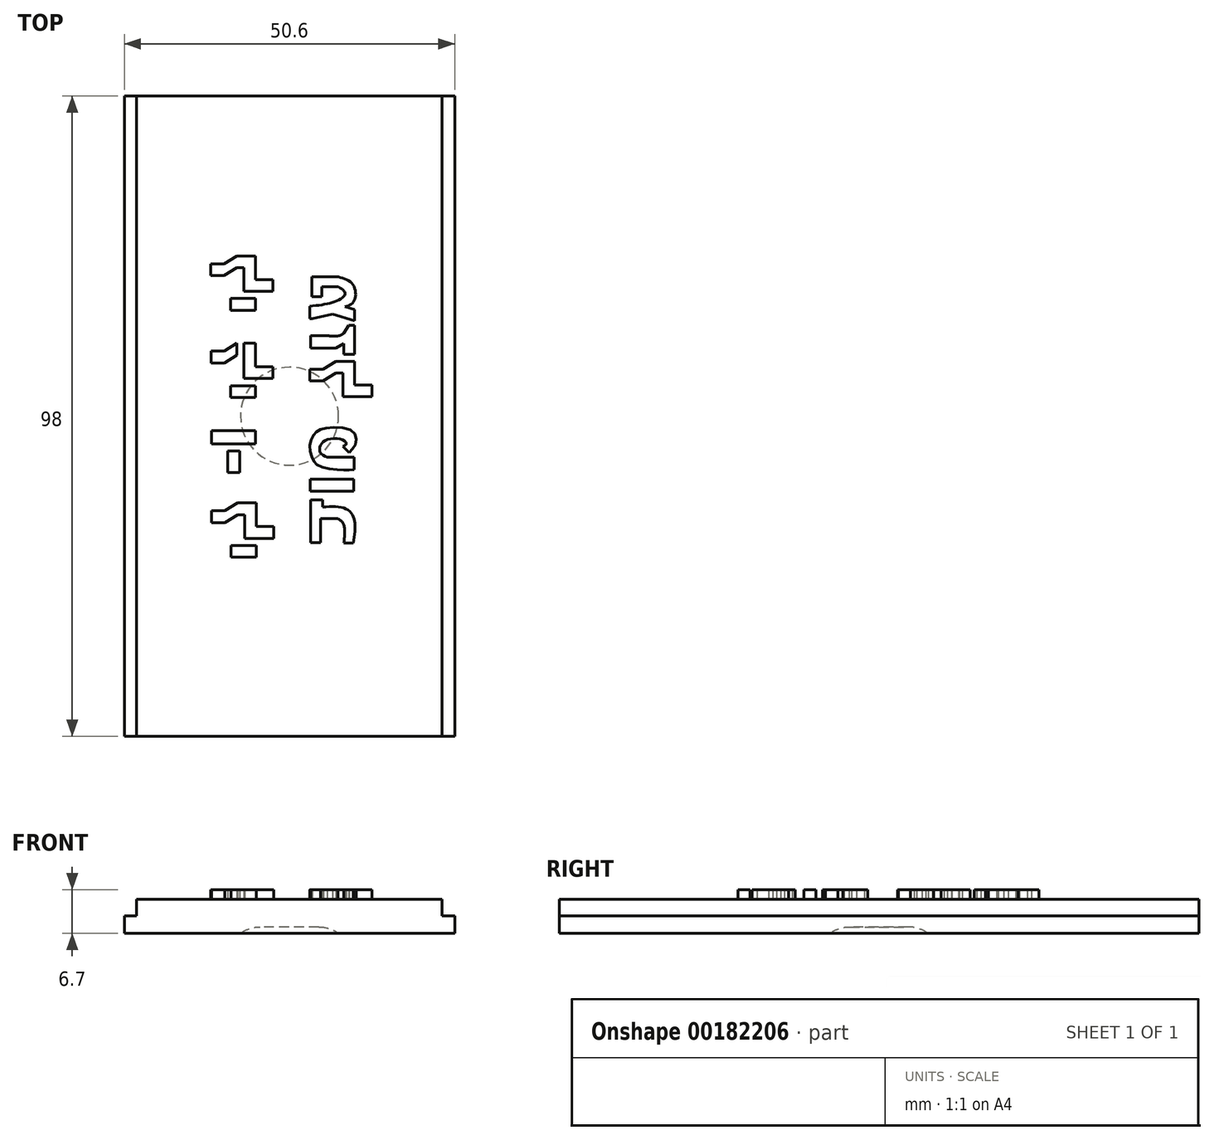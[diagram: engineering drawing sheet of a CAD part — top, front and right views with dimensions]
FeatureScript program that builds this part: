
annotation { "Feature Type Name" : "Feature", "Feature Type Description" : "" }
export const myFeature = defineFeature(function(context is Context, id is Id, definition is map)
    precondition{}
    {
        {
            var Q0;
            Q0=qCreatedBy(makeId("Front.planeOp"),FACE);
            var sketch = newSketch(context, id + "F0", { "sketchPlane" : qUnion([Q0])});
            skLineSegment(sketch, "E0.bottom", {"start": v(25.3, 1.35) * mm, "end": v(-25.3, 1.35) * mm});
            skLineSegment(sketch, "E0.top", {"start": v(25.3, -1.35) * mm, "end": v(-25.3, -1.35) * mm});
            skLineSegment(sketch, "E0.left", {"start": v(25.3, 1.35) * mm, "end": v(25.3, -1.35) * mm});
            skLineSegment(sketch, "E0.right", {"start": v(-25.3, 1.35) * mm, "end": v(-25.3, -1.35) * mm});
            skPoint(sketch, "E0.middle", {"position": v(0, 0) * mm});
            skLineSegment(sketch, "E1", {"start": v(-25.3, 1.35) * mm, "end": v(-23.45, 1.35) * mm});
            skLineSegment(sketch, "E2", {"start": v(25.3, 1.35) * mm, "end": v(23.35, 1.35) * mm});
            skLineSegment(sketch, "E3", {"start": v(-23.45, 1.35) * mm, "end": v(-23.45, 3.85) * mm});
            skLineSegment(sketch, "E4", {"start": v(-23.45, 3.85) * mm, "end": v(23.35, 3.85) * mm});
            skLineSegment(sketch, "E5", {"start": v(23.35, 3.85) * mm, "end": v(23.35, 1.35) * mm});
            skSolve(sketch);
        }
        {
            var Q0;
            Q0=makeQuery(id+"F0.imprint","IMPRINT",FACE,{"disambiguationData":[TD([[makeQuery(id+"F0.imprint","IMPRINT",EDGE,{"derivedFrom":sQuery(id+"F0.wireOp",EDGE,"E0.bottom")}),1.0]])]});
            var Q1;
            Q1=makeQuery(id+"F0.imprint","IMPRINT",FACE,{"disambiguationData":[TD([[makeQuery(id+"F0.imprint","IMPRINT",EDGE,{"derivedFrom":sQuery(id+"F0.wireOp",EDGE,"E0.bottom")}),-1.0]])]});
            extrude(context, id + "F1", {"entities" : qUnion([Q0, Q1]), "endBound" : BoundingType.SYMMETRIC, "depth" : 98 * mm});
        }
        {
            var Q0;
            Q0=qCreatedBy(makeId("Front.planeOp"),FACE);
            var sketch = newSketch(context, id + "F2", { "sketchPlane" : qUnion([Q0])});
            skLineSegment(sketch, "E6.bottom", {"start": v(0, -0.35) * mm, "end": v(7.5, -0.35) * mm});
            skLineSegment(sketch, "E6.top", {"start": v(0, -1.35) * mm, "end": v(7.5, -1.35) * mm});
            skLineSegment(sketch, "E6.left", {"start": v(0, -0.35) * mm, "end": v(0, -1.35) * mm});
            skLineSegment(sketch, "E6.right", {"start": v(7.5, -0.35) * mm, "end": v(7.5, -1.35) * mm});
            skSolve(sketch);
        }
        {
            var Q0;
            Q0=qSketchRegion(id+"F2",true);
            var Q1;
            Q1=sQuery(id+"F2.wireOp",EDGE,"E6.left");
            revolve(context, id + "F3", {"operationType" : NewBodyOperationType.REMOVE, "entities" : qUnion([Q0]), "axis" : qUnion([Q1]), "revolveType" : RevolveType.FULL});
        }
        {
            var Q0;
            Q0=makeQuery(id+"F3.boolean.opBoolean","COPY",EDGE,{"derivedFrom":makeQuery(id+"F3.opRevolve","SWEPT_EDGE",EDGE,{"disambiguationData":[OSD([sQuery(id+"F2.wireOp",EDGE,"E6.bottom"),sQuery(id+"F2.wireOp",EDGE,"E6.right")])]})});
            fillet(context, id + "F4", {"entities" : qUnion([Q0]), "radius" : 5 * mm, "tangentPropagation" : true, "allowEdgeOverflow" : false});
        }
        {
            var Q0;
            Q0=makeQuery(id+"F1.opExtrude","SWEPT_FACE",FACE,{"disambiguationData":[OSD([sQuery(id+"F0.wireOp",EDGE,"E4")])]});
            var sketch = newSketch(context, id + "F5", { "sketchPlane" : qUnion([Q0])});
            skLineSegment(sketch, "E7.MirrorCS", {"start": v(-5.1, -21.59) * mm, "end": v(-8.93, -21.59) * mm});
            skLineSegment(sketch, "E8.MirrorCS", {"start": v(-5.1, -21.59) * mm, "end": v(-5.1, -19.78) * mm});
            skLineSegment(sketch, "E9.MirrorCS", {"start": v(-5.1, -19.78) * mm, "end": v(-8.93, -19.78) * mm});
            skLineSegment(sketch, "E10.MirrorCS", {"start": v(-8.93, -21.59) * mm, "end": v(-8.93, -19.78) * mm});
            skLineSegment(sketch, "E11.MirrorCS", {"start": v(-2.43, -18.7) * mm, "end": v(-6.89, -18.7) * mm});
            skLineSegment(sketch, "E12.MirrorCS", {"start": v(-2.43, -18.7) * mm, "end": v(-2.43, -16.9) * mm});
            skLineSegment(sketch, "E13.MirrorCS", {"start": v(-2.43, -16.9) * mm, "end": v(-6.89, -16.9) * mm});
            skLineSegment(sketch, "E14.MirrorCS", {"start": v(-6.89, -18.7) * mm, "end": v(-6.89, -16.9) * mm});
            skLineSegment(sketch, "E15.MirrorCS", {"start": v(-6.89, -16.9) * mm, "end": v(-6.89, -13.28) * mm});
            skLineSegment(sketch, "E16.MirrorCS", {"start": v(-5.1, -16.9) * mm, "end": v(-5.1, -13.28) * mm});
            skLineSegment(sketch, "E17.MirrorCS", {"start": v(-6.89, -13.28) * mm, "end": v(-5.1, -13.28) * mm});
            skLineSegment(sketch, "E18.MirrorCS", {"start": v(-6.89, -15.09) * mm, "end": v(-7.97, -15.09) * mm});
            skLineSegment(sketch, "E19.MirrorCS", {"start": v(-6.89, -13.28) * mm, "end": v(-7.97, -13.28) * mm});
            skLineSegment(sketch, "E20.MirrorCS", {"start": v(-9.9, -16.29) * mm, "end": v(-7.97, -15.09) * mm});
            skLineSegment(sketch, "E21.MirrorCS", {"start": v(-7.97, -13.28) * mm, "end": v(-9.9, -14.48) * mm});
            skLineSegment(sketch, "E22.MirrorCS", {"start": v(-11.94, -16.29) * mm, "end": v(-11.94, -14.48) * mm});
            skLineSegment(sketch, "E23.MirrorCS", {"start": v(-9.9, -16.29) * mm, "end": v(-11.94, -16.29) * mm});
            skLineSegment(sketch, "E24.MirrorCS", {"start": v(-9.9, -14.48) * mm, "end": v(-11.94, -14.48) * mm});
            skLineSegment(sketch, "E25.MirrorCS", {"start": v(-5.19, -2.22) * mm, "end": v(-11.97, -2.22) * mm});
            skLineSegment(sketch, "E26.MirrorCS", {"start": v(-5.19, -4.22) * mm, "end": v(-11.97, -4.22) * mm});
            skLineSegment(sketch, "E27.MirrorCS", {"start": v(-11.97, -4.22) * mm, "end": v(-11.97, -2.22) * mm});
            skLineSegment(sketch, "E28.MirrorCS", {"start": v(-5.19, -4.22) * mm, "end": v(-5.19, -2.22) * mm});
            skLineSegment(sketch, "E29.MirrorCS", {"start": v(-7.64, -8.65) * mm, "end": v(-9.48, -8.65) * mm});
            skLineSegment(sketch, "E30.MirrorCS", {"start": v(-7.64, -8.65) * mm, "end": v(-7.64, -5.33) * mm});
            skLineSegment(sketch, "E31.MirrorCS", {"start": v(-9.48, -8.65) * mm, "end": v(-9.48, -5.33) * mm});
            skLineSegment(sketch, "E32.MirrorCS", {"start": v(-7.64, -5.33) * mm, "end": v(-9.48, -5.33) * mm});
            skLineSegment(sketch, "E33.MirrorCS", {"start": v(-5.19, 2.87) * mm, "end": v(-9.02, 2.87) * mm});
            skLineSegment(sketch, "E34.MirrorCS", {"start": v(-5.19, 2.87) * mm, "end": v(-5.19, 4.67) * mm});
            skLineSegment(sketch, "E35.MirrorCS", {"start": v(-9.02, 2.87) * mm, "end": v(-9.02, 4.67) * mm});
            skLineSegment(sketch, "E36.MirrorCS", {"start": v(-5.19, 4.67) * mm, "end": v(-9.02, 4.67) * mm});
            skLineSegment(sketch, "E37.MirrorCS", {"start": v(-2.52, 5.76) * mm, "end": v(-6.98, 5.76) * mm});
            skLineSegment(sketch, "E38.MirrorCS", {"start": v(-2.52, 5.76) * mm, "end": v(-2.52, 7.56) * mm});
            skLineSegment(sketch, "E39.MirrorCS", {"start": v(-6.98, 5.76) * mm, "end": v(-6.98, 7.56) * mm});
            skLineSegment(sketch, "E40.MirrorCS", {"start": v(-5.19, 7.56) * mm, "end": v(-5.19, 11.17) * mm});
            skLineSegment(sketch, "E41.MirrorCS", {"start": v(-6.98, 7.56) * mm, "end": v(-6.98, 11.17) * mm});
            skLineSegment(sketch, "E42.MirrorCS", {"start": v(-6.98, 7.56) * mm, "end": v(-5.19, 7.56) * mm});
            skLineSegment(sketch, "E43.MirrorCS", {"start": v(-2.52, 7.56) * mm, "end": v(-6.98, 7.56) * mm});
            skLineSegment(sketch, "E44.MirrorCS", {"start": v(-6.98, 11.17) * mm, "end": v(-6.98, 9.37) * mm});
            skLineSegment(sketch, "E45.MirrorCS", {"start": v(-8.06, 11.17) * mm, "end": v(-8.06, 9.37) * mm});
            skLineSegment(sketch, "E46.MirrorCS", {"start": v(-6.98, 11.17) * mm, "end": v(-8.06, 11.17) * mm});
            skLineSegment(sketch, "E47.MirrorCS", {"start": v(-6.98, 9.37) * mm, "end": v(-8.06, 9.37) * mm});
            skLineSegment(sketch, "E48.MirrorCS", {"start": v(-8.06, 11.17) * mm, "end": v(-9.99, 9.97) * mm});
            skLineSegment(sketch, "E49.MirrorCS", {"start": v(-9.99, 8.16) * mm, "end": v(-8.06, 9.37) * mm});
            skLineSegment(sketch, "E50.MirrorCS", {"start": v(-9.99, 8.16) * mm, "end": v(-12.03, 8.16) * mm});
            skLineSegment(sketch, "E51.MirrorCS", {"start": v(-9.99, 9.97) * mm, "end": v(-12.03, 9.97) * mm});
            skLineSegment(sketch, "E52.MirrorCS", {"start": v(-12.03, 8.16) * mm, "end": v(-12.03, 9.97) * mm});
            skLineSegment(sketch, "E53.MirrorCS", {"start": v(-6.98, 11.17) * mm, "end": v(-5.19, 11.17) * mm});
            skLineSegment(sketch, "E54.MirrorCS", {"start": v(-2.55, 19.11) * mm, "end": v(-2.55, 20.92) * mm});
            skLineSegment(sketch, "E55.MirrorCS", {"start": v(-2.55, 19.11) * mm, "end": v(-7, 19.11) * mm});
            skLineSegment(sketch, "E56.MirrorCS", {"start": v(-2.55, 20.92) * mm, "end": v(-7, 20.92) * mm});
            skLineSegment(sketch, "E57.MirrorCS", {"start": v(-5.22, 20.92) * mm, "end": v(-5.22, 24.53) * mm});
            skLineSegment(sketch, "E58.MirrorCS", {"start": v(-7, 24.53) * mm, "end": v(-5.22, 24.53) * mm});
            skLineSegment(sketch, "E59.MirrorCS", {"start": v(-7, 20.92) * mm, "end": v(-7, 24.53) * mm});
            skLineSegment(sketch, "E60.MirrorCS", {"start": v(-7, 19.11) * mm, "end": v(-7, 20.92) * mm});
            skLineSegment(sketch, "E61.MirrorCS", {"start": v(-7, 22.72) * mm, "end": v(-8.09, 22.72) * mm});
            skLineSegment(sketch, "E62.MirrorCS", {"start": v(-7, 24.53) * mm, "end": v(-8.09, 24.53) * mm});
            skLineSegment(sketch, "E63.MirrorCS", {"start": v(-8.09, 24.53) * mm, "end": v(-10.02, 23.33) * mm});
            skLineSegment(sketch, "E64.MirrorCS", {"start": v(-10.02, 21.52) * mm, "end": v(-8.09, 22.72) * mm});
            skLineSegment(sketch, "E65.MirrorCS", {"start": v(-10.02, 21.52) * mm, "end": v(-12.06, 21.52) * mm});
            skLineSegment(sketch, "E66.MirrorCS", {"start": v(-10.02, 23.33) * mm, "end": v(-12.06, 23.33) * mm});
            skLineSegment(sketch, "E67.MirrorCS", {"start": v(-12.06, 21.52) * mm, "end": v(-12.06, 23.33) * mm});
            skLineSegment(sketch, "E68.MirrorCS", {"start": v(-5.22, 18.03) * mm, "end": v(-9.05, 18.03) * mm});
            skLineSegment(sketch, "E69.MirrorCS", {"start": v(-9.05, 16.22) * mm, "end": v(-9.05, 18.03) * mm});
            skLineSegment(sketch, "E70.MirrorCS", {"start": v(-5.22, 16.22) * mm, "end": v(-9.05, 16.22) * mm});
            skLineSegment(sketch, "E71.MirrorCS", {"start": v(-5.22, 16.22) * mm, "end": v(-5.22, 18.03) * mm});
            skFitSpline(sketch, "E72.MirrorCS", {"points": [v(7.5, 19.8) * mm, v(8.5, 18.86) * mm, v(7.5, 17.76) * mm, v(3.11, 16.82) * mm], "startDerivative": vector(5.52, -3.39) * mm, "endDerivative": vector(-10.58, -1.26) * mm});
            skLineSegment(sketch, "E73.MirrorCS", {"start": v(4.92, 19.8) * mm, "end": v(7.5, 19.8) * mm});
            skLineSegment(sketch, "E74.MirrorCS", {"start": v(4.92, 18.27) * mm, "end": v(4.92, 19.8) * mm});
            skLineSegment(sketch, "E75.MirrorCS", {"start": v(3.4, 18.27) * mm, "end": v(4.92, 18.27) * mm});
            skLineSegment(sketch, "E76.MirrorCS", {"start": v(3.4, 21.33) * mm, "end": v(3.4, 18.27) * mm});
            skLineSegment(sketch, "E77.MirrorCS", {"start": v(7.5, 21.33) * mm, "end": v(3.4, 21.33) * mm});
            skFitSpline(sketch, "E78.MirrorCS", {"points": [v(8.53, 16.75) * mm, v(9.86, 17.59) * mm, v(9.78, 20.06) * mm, v(7.5, 21.33) * mm], "startDerivative": vector(5.55, 1.8) * mm, "endDerivative": vector(-7.52, 2.27) * mm});
            skLineSegment(sketch, "E79.MirrorCS", {"start": v(9.96, 14.6) * mm, "end": v(9.96, 16.3) * mm});
            skLineSegment(sketch, "E80.MirrorCS", {"start": v(9.96, 16.3) * mm, "end": v(8.53, 16.75) * mm});
            skLineSegment(sketch, "E81.MirrorCS", {"start": v(6.62, 15.63) * mm, "end": v(9.96, 14.6) * mm});
            skFitSpline(sketch, "E82.MirrorCS", {"points": [v(3.48, 14.95) * mm, v(6.62, 15.63) * mm], "startDerivative": vector(3.15, 0.68) * mm, "endDerivative": vector(3.15, 0.68) * mm});
            skLineSegment(sketch, "E83.MirrorCS", {"start": v(3.11, 16.82) * mm, "end": v(3.11, 14.95) * mm});
            skLineSegment(sketch, "E84.MirrorCS", {"start": v(3.48, 14.95) * mm, "end": v(3.11, 14.95) * mm});
            skFitSpline(sketch, "E85.MirrorCS", {"points": [v(3.48, 14.95) * mm, v(6.62, 15.63) * mm], "startDerivative": vector(3.15, 0.68) * mm, "endDerivative": vector(3.15, 0.68) * mm});
            skLineSegment(sketch, "E86.MirrorCS", {"start": v(3.22, 12.3) * mm, "end": v(5.18, 12.3) * mm});
            skFitSpline(sketch, "E87.MirrorCS", {"points": [v(5.18, 12.3) * mm, v(5.95, 12.3) * mm, v(7.5, 12.3) * mm, v(8.33, 12.73) * mm], "startDerivative": vector(2.37, 0.09) * mm, "endDerivative": vector(2.29, 1.69) * mm});
            skFitSpline(sketch, "E88.MirrorCS", {"points": [v(8.33, 12.73) * mm, v(9.06, 13.93) * mm], "startDerivative": vector(0.73, 1.2) * mm, "endDerivative": vector(0.73, 1.2) * mm});
            skLineSegment(sketch, "E89.MirrorCS", {"start": v(9.96, 13.93) * mm, "end": v(9.06, 13.93) * mm});
            skLineSegment(sketch, "E90.MirrorCS", {"start": v(9.96, 13.93) * mm, "end": v(9.96, 9.5) * mm});
            skLineSegment(sketch, "E91.MirrorCS", {"start": v(9.96, 9.5) * mm, "end": v(9.06, 9.5) * mm});
            skLineSegment(sketch, "E92.MirrorCS", {"start": v(9.06, 9.5) * mm, "end": v(8.33, 9.5) * mm});
            skLineSegment(sketch, "E93.MirrorCS", {"start": v(8.33, 9.5) * mm, "end": v(8.33, 12.73) * mm});
            skFitSpline(sketch, "E94.MirrorCS", {"points": [v(7.09, 10.43) * mm, v(5.67, 10.43) * mm, v(3.99, 10.43) * mm], "startDerivative": vector(-2.9, 0) * mm, "endDerivative": vector(-3.29, 0) * mm});
            skLineSegment(sketch, "E95.MirrorCS", {"start": v(3.99, 10.43) * mm, "end": v(3.22, 10.43) * mm});
            skLineSegment(sketch, "E96.MirrorCS", {"start": v(3.22, 10.43) * mm, "end": v(3.22, 12.3) * mm});
            skFitSpline(sketch, "E97.MirrorCS", {"points": [v(7.09, 10.43) * mm, v(8.33, 11.12) * mm], "startDerivative": vector(1.24, 0.68) * mm, "endDerivative": vector(1.24, 0.68) * mm});
            skLineSegment(sketch, "E98.MirrorCS", {"start": v(7.09, 8.4) * mm, "end": v(5.16, 7.2) * mm});
            skLineSegment(sketch, "E99.MirrorCS", {"start": v(5.16, 5.39) * mm, "end": v(7.09, 6.59) * mm});
            skLineSegment(sketch, "E100.MirrorCS", {"start": v(5.16, 5.39) * mm, "end": v(3.11, 5.39) * mm});
            skLineSegment(sketch, "E101.MirrorCS", {"start": v(5.16, 7.2) * mm, "end": v(3.11, 7.2) * mm});
            skLineSegment(sketch, "E102.MirrorCS", {"start": v(3.11, 5.39) * mm, "end": v(3.11, 7.2) * mm});
            skLineSegment(sketch, "E103.MirrorCS", {"start": v(5.16, 5.39) * mm, "end": v(5.16, 7.2) * mm});
            skLineSegment(sketch, "E104.MirrorCS", {"start": v(8.17, 6.59) * mm, "end": v(7.09, 6.59) * mm});
            skLineSegment(sketch, "E105.MirrorCS", {"start": v(8.17, 8.4) * mm, "end": v(7.09, 8.4) * mm});
            skLineSegment(sketch, "E106.MirrorCS", {"start": v(8.17, 8.4) * mm, "end": v(9.96, 8.4) * mm});
            skLineSegment(sketch, "E107.MirrorCS", {"start": v(9.96, 4.78) * mm, "end": v(9.96, 8.4) * mm});
            skLineSegment(sketch, "E108.MirrorCS", {"start": v(12.63, 4.78) * mm, "end": v(8.17, 4.78) * mm});
            skLineSegment(sketch, "E109.MirrorCS", {"start": v(8.17, 4.78) * mm, "end": v(8.17, 8.4) * mm});
            skLineSegment(sketch, "E110.MirrorCS", {"start": v(8.17, 2.98) * mm, "end": v(8.17, 4.78) * mm});
            skLineSegment(sketch, "E111.MirrorCS", {"start": v(12.63, 2.98) * mm, "end": v(8.17, 2.98) * mm});
            skLineSegment(sketch, "E112.MirrorCS", {"start": v(12.63, 2.98) * mm, "end": v(12.63, 4.78) * mm});
            skFitSpline(sketch, "E113.MirrorCS", {"points": [v(9.16, -5.56) * mm, v(10.12, -4.24) * mm, v(9.64, -2.31) * mm, v(5.42, -1.83) * mm, v(3.98, -2.55) * mm, v(3.14, -4.24) * mm, v(3.5, -6.4) * mm, v(4.46, -7.6) * mm, v(7.95, -8.21) * mm, v(9.88, -8.21) * mm], "startDerivative": vector(12.28, 12.03) * mm, "endDerivative": vector(16.13, 0.48) * mm});
            skLineSegment(sketch, "E114.MirrorCS", {"start": v(9.88, -8.21) * mm, "end": v(9.88, -6.28) * mm});
            skLineSegment(sketch, "E115.MirrorCS", {"start": v(5.79, -6.28) * mm, "end": v(9.64, -6.28) * mm});
            skLineSegment(sketch, "E116.MirrorCS", {"start": v(9.88, -6.28) * mm, "end": v(9.64, -6.28) * mm});
            skFitSpline(sketch, "E117.MirrorCS", {"points": [v(5.79, -6.28) * mm, v(4.7, -5.56) * mm, v(4.7, -4.6) * mm, v(5.67, -3.64) * mm, v(8.2, -3.64) * mm, v(8.68, -4.24) * mm, v(8.2, -4.6) * mm], "startDerivative": vector(-7.7, 3.48) * mm, "endDerivative": vector(-5.56, -2.54) * mm});
            skLineSegment(sketch, "E118.MirrorCS", {"start": v(9.16, -5.56) * mm, "end": v(8.2, -4.6) * mm});
            skLineSegment(sketch, "E119.MirrorCS", {"start": v(9.82, -9.66) * mm, "end": v(3.18, -9.66) * mm});
            skLineSegment(sketch, "E120.MirrorCS", {"start": v(3.18, -11.5) * mm, "end": v(3.18, -9.66) * mm});
            skLineSegment(sketch, "E121.MirrorCS", {"start": v(9.82, -11.5) * mm, "end": v(3.18, -11.5) * mm});
            skLineSegment(sketch, "E122.MirrorCS", {"start": v(9.82, -11.5) * mm, "end": v(9.82, -9.66) * mm});
            skLineSegment(sketch, "E123.MirrorCS", {"start": v(3.22, -12.8) * mm, "end": v(3.22, -19.37) * mm});
            skLineSegment(sketch, "E124.MirrorCS", {"start": v(4.75, -15.7) * mm, "end": v(7.4, -15.7) * mm});
            skLineSegment(sketch, "E125.MirrorCS", {"start": v(4.75, -19.37) * mm, "end": v(4.75, -15.7) * mm});
            skLineSegment(sketch, "E126.MirrorCS", {"start": v(3.22, -19.37) * mm, "end": v(4.75, -19.37) * mm});
            skFitSpline(sketch, "E127.MirrorCS", {"points": [v(7.4, -15.7) * mm, v(8.24, -16.47) * mm, v(8.33, -19.45) * mm], "startDerivative": vector(2.62, -1.46) * mm, "endDerivative": vector(-0.5, -5.7) * mm});
            skLineSegment(sketch, "E128.MirrorCS", {"start": v(9.78, -19.45) * mm, "end": v(8.33, -19.45) * mm});
            skFitSpline(sketch, "E129.MirrorCS", {"points": [v(9.78, -19.45) * mm, v(10.03, -16.64) * mm, v(9.6, -15.02) * mm, v(8.16, -14) * mm, v(5.1, -13.92) * mm], "startDerivative": vector(1.5, 10.74) * mm, "endDerivative": vector(-11.49, -0.83) * mm});
            skLineSegment(sketch, "E130.MirrorCS", {"start": v(5.1, -13.92) * mm, "end": v(5.1, -12.8) * mm});
            skLineSegment(sketch, "E131.MirrorCS", {"start": v(5.1, -12.8) * mm, "end": v(3.22, -12.8) * mm});
            skSolve(sketch);
        }
        {
            var Q0;
            Q0=makeQuery(id+"F5.imprint","IMPRINT",FACE,{"disambiguationData":[TD([[makeQuery(id+"F5.imprint","IMPRINT",EDGE,{"derivedFrom":sQuery(id+"F5.wireOp",EDGE,"E72.MirrorCS")}),1.0]])]});
            var Q1;
            Q1=makeQuery(id+"F5.imprint","IMPRINT",FACE,{"disambiguationData":[TD([[makeQuery(id+"F5.imprint","IMPRINT",EDGE,{"derivedFrom":sQuery(id+"F5.wireOp",EDGE,"E86.MirrorCS")}),-1.0]])]});
            var Q2;
            {var subQ0=sQuery(id+"F5.wireOp",EDGE,"E88.MirrorCS");Q2=makeQuery(id+"F5.imprint","IMPRINT",FACE,{"disambiguationData":[TD([[makeQuery(id+"F5.imprint","IMPRINT",EDGE,{"derivedFrom":subQ0}),-1.0]])]});}
            var Q3;
            Q3=makeQuery(id+"F5.imprint","IMPRINT",FACE,{"disambiguationData":[TD([[makeQuery(id+"F5.imprint","IMPRINT",EDGE,{"derivedFrom":sQuery(id+"F5.wireOp",EDGE,"E98.MirrorCS")}),1.0]])]});
            var Q4;
            Q4=makeQuery(id+"F5.imprint","IMPRINT",FACE,{"disambiguationData":[TD([[makeQuery(id+"F5.imprint","IMPRINT",EDGE,{"derivedFrom":sQuery(id+"F5.wireOp",EDGE,"E100.MirrorCS")}),-1.0]])]});
            var Q5;
            {var subQ5=sQuery(id+"F5.wireOp",EDGE,"E106.MirrorCS");Q5=makeQuery(id+"F5.imprint","IMPRINT",FACE,{"disambiguationData":[TD([[makeQuery(id+"F5.imprint","IMPRINT",EDGE,{"derivedFrom":subQ5}),-1.0]])]});}
            var Q6;
            {var subQ0=sQuery(id+"F5.wireOp",EDGE,"E110.MirrorCS");Q6=makeQuery(id+"F5.imprint","IMPRINT",FACE,{"disambiguationData":[TD([[makeQuery(id+"F5.imprint","IMPRINT",EDGE,{"derivedFrom":subQ0}),-1.0]])]});}
            var Q7;
            Q7=makeQuery(id+"F5.imprint","IMPRINT",FACE,{"disambiguationData":[TD([[makeQuery(id+"F5.imprint","IMPRINT",EDGE,{"derivedFrom":sQuery(id+"F5.wireOp",EDGE,"E114.MirrorCS")}),1.0]])]});
            var Q8;
            Q8=makeQuery(id+"F5.imprint","IMPRINT",FACE,{"disambiguationData":[TD([[makeQuery(id+"F5.imprint","IMPRINT",EDGE,{"derivedFrom":sQuery(id+"F5.wireOp",EDGE,"E119.MirrorCS")}),1.0]])]});
            var Q9;
            Q9=makeQuery(id+"F5.imprint","IMPRINT",FACE,{"disambiguationData":[TD([[makeQuery(id+"F5.imprint","IMPRINT",EDGE,{"derivedFrom":sQuery(id+"F5.wireOp",EDGE,"E123.MirrorCS")}),1.0]])]});
            var Q10;
            {var subQ1=sQuery(id+"F5.wireOp",EDGE,"E61.MirrorCS");Q10=makeQuery(id+"F5.imprint","IMPRINT",FACE,{"disambiguationData":[TD([[makeQuery(id+"F5.imprint","IMPRINT",EDGE,{"derivedFrom":subQ1}),-1.0]])]});}
            var Q11;
            {var subQ5=sQuery(id+"F5.wireOp",EDGE,"E57.MirrorCS");Q11=makeQuery(id+"F5.imprint","IMPRINT",FACE,{"disambiguationData":[TD([[makeQuery(id+"F5.imprint","IMPRINT",EDGE,{"derivedFrom":subQ5}),1.0]])]});}
            var Q12;
            {var subQ3=sQuery(id+"F5.wireOp",EDGE,"E54.MirrorCS");Q12=makeQuery(id+"F5.imprint","IMPRINT",FACE,{"disambiguationData":[TD([[makeQuery(id+"F5.imprint","IMPRINT",EDGE,{"derivedFrom":subQ3}),1.0]])]});}
            var Q13;
            Q13=makeQuery(id+"F5.imprint","IMPRINT",FACE,{"disambiguationData":[TD([[makeQuery(id+"F5.imprint","IMPRINT",EDGE,{"derivedFrom":sQuery(id+"F5.wireOp",EDGE,"E68.MirrorCS")}),1.0]])]});
            var Q14;
            Q14=makeQuery(id+"F5.imprint","IMPRINT",FACE,{"disambiguationData":[TD([[makeQuery(id+"F5.imprint","IMPRINT",EDGE,{"derivedFrom":sQuery(id+"F5.wireOp",EDGE,"E45.MirrorCS")}),-1.0]])]});
            var Q15;
            Q15=makeQuery(id+"F5.imprint","IMPRINT",FACE,{"disambiguationData":[TD([[makeQuery(id+"F5.imprint","IMPRINT",EDGE,{"derivedFrom":sQuery(id+"F5.wireOp",EDGE,"E44.MirrorCS")}),-1.0]])]});
            var Q16;
            {var subQ2=sQuery(id+"F5.wireOp",EDGE,"E40.MirrorCS");Q16=makeQuery(id+"F5.imprint","IMPRINT",FACE,{"disambiguationData":[TD([[makeQuery(id+"F5.imprint","IMPRINT",EDGE,{"derivedFrom":subQ2}),1.0]])]});}
            var Q17;
            {var subQ1=sQuery(id+"F5.wireOp",EDGE,"E38.MirrorCS");Q17=makeQuery(id+"F5.imprint","IMPRINT",FACE,{"disambiguationData":[TD([[makeQuery(id+"F5.imprint","IMPRINT",EDGE,{"derivedFrom":subQ1}),1.0]])]});}
            var Q18;
            Q18=makeQuery(id+"F5.imprint","IMPRINT",FACE,{"disambiguationData":[TD([[makeQuery(id+"F5.imprint","IMPRINT",EDGE,{"derivedFrom":sQuery(id+"F5.wireOp",EDGE,"E33.MirrorCS")}),-1.0]])]});
            var Q19;
            Q19=makeQuery(id+"F5.imprint","IMPRINT",FACE,{"disambiguationData":[TD([[makeQuery(id+"F5.imprint","IMPRINT",EDGE,{"derivedFrom":sQuery(id+"F5.wireOp",EDGE,"E25.MirrorCS")}),1.0]])]});
            var Q20;
            Q20=makeQuery(id+"F5.imprint","IMPRINT",FACE,{"disambiguationData":[TD([[makeQuery(id+"F5.imprint","IMPRINT",EDGE,{"derivedFrom":sQuery(id+"F5.wireOp",EDGE,"E30.MirrorCS")}),1.0]])]});
            var Q21;
            {var subQ1=sQuery(id+"F5.wireOp",EDGE,"E18.MirrorCS");Q21=makeQuery(id+"F5.imprint","IMPRINT",FACE,{"disambiguationData":[TD([[makeQuery(id+"F5.imprint","IMPRINT",EDGE,{"derivedFrom":subQ1}),-1.0]])]});}
            var Q22;
            {var subQ5=sQuery(id+"F5.wireOp",EDGE,"E16.MirrorCS");Q22=makeQuery(id+"F5.imprint","IMPRINT",FACE,{"disambiguationData":[TD([[makeQuery(id+"F5.imprint","IMPRINT",EDGE,{"derivedFrom":subQ5}),1.0]])]});}
            var Q23;
            Q23=makeQuery(id+"F5.imprint","IMPRINT",FACE,{"disambiguationData":[TD([[makeQuery(id+"F5.imprint","IMPRINT",EDGE,{"derivedFrom":sQuery(id+"F5.wireOp",EDGE,"E11.MirrorCS")}),-1.0]])]});
            var Q24;
            Q24=makeQuery(id+"F5.imprint","IMPRINT",FACE,{"disambiguationData":[TD([[makeQuery(id+"F5.imprint","IMPRINT",EDGE,{"derivedFrom":sQuery(id+"F5.wireOp",EDGE,"E7.MirrorCS")}),-1.0]])]});
            extrude(context, id + "F6", {"entities" : qUnion([Q0, Q1, Q2, Q3, Q4, Q5, Q6, Q7, Q8, Q9, Q10, Q11, Q12, Q13, Q14, Q15, Q16, Q17, Q18, Q19, Q20, Q21, Q22, Q23, Q24]), "operationType" : NewBodyOperationType.ADD, "depth" : 1.5 * mm});
        }
    });
